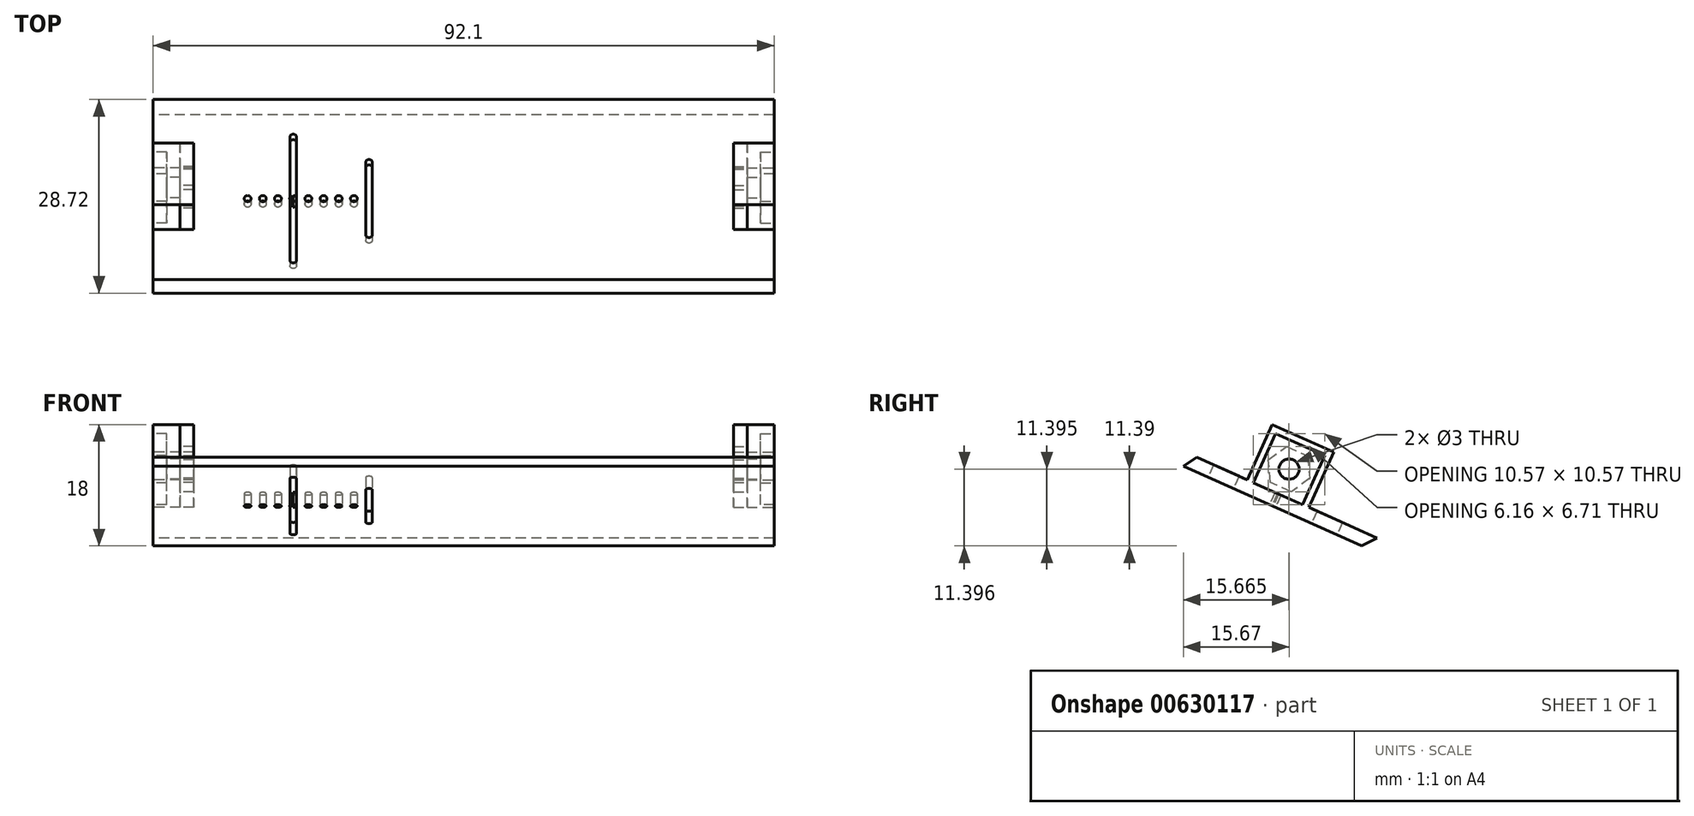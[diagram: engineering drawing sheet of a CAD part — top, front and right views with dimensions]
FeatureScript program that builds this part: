
annotation { "Feature Type Name" : "Feature", "Feature Type Description" : "" }
export const myFeature = defineFeature(function(context is Context, id is Id, definition is map)
    precondition{}
    {
        {
            var Q0;
            Q0=qCreatedBy(makeId("Right.planeOp"),FACE);
            var sketch = newSketch(context, id + "F0", { "sketchPlane" : qUnion([Q0])});
            skLineSegment(sketch, "E0.6", {"start": v(14.9, 8.68) * mm, "end": v(-11.53, 20.52) * mm});
            skLineSegment(sketch, "E1.2", {"start": v(17.19, 9.85) * mm, "end": v(-9.53, 21.81) * mm});
            skLineSegment(sketch, "E2", {"start": v(17.19, 9.85) * mm, "end": v(14.9, 8.68) * mm});
            skLineSegment(sketch, "E3", {"start": v(-9.53, 21.81) * mm, "end": v(-11.53, 20.52) * mm});
            skSolve(sketch);
        }
        {
            var Q0;
            Q0 = qSketchRegion(id + "F0", true);
            extrude(context, id + "F1", {"entities" : qUnion([Q0]), "depth" : 92.1 * mm, "offsetDistance" : 25 * mm, "symmetric" : true});
        }
        {
            var Q0;
            Q0=makeQuery(id+"F1.opExtrude","CAP_FACE",FACE,{"disambiguationData":[OSD([sQuery(id+"F0.wireOp",EDGE,"E0.6"),sQuery(id+"F0.wireOp",EDGE,"E1.2"),sQuery(id+"F0.wireOp",EDGE,"E2"),sQuery(id+"F0.wireOp",EDGE,"E3")])],"isStart":true});
            var sketch = newSketch(context, id + "F2", { "sketchPlane" : qUnion([Q0])});
            skPoint(sketch, "E4", {"position": v(-1.69, 14.6) * mm});
            skLineSegment(sketch, "E5", {"start": v(-1.69, 14.6) * mm, "end": v(-2.91, 17.34) * mm, "construction": true});
            skLineSegment(sketch, "E6", {"start": v(-2.91, 17.34) * mm, "end": v(-5.36, 22.81) * mm, "construction": true});
            skPoint(sketch, "E7", {"position": v(-4.14, 20.07) * mm});
            skCircle(sketch, "E8", {"center": v(-4.14, 20.07) * mm, "radius": 1.5 * mm});
            skCircle(sketch, "E9", {"center": v(-4.14, 20.07) * mm, "radius": 2.75 * mm, "construction": true});
            skLineSegment(sketch, "E10.bottom", {"start": v(-5.65, 16.1) * mm, "end": v(-8.1, 21.58) * mm, "construction": true});
            skLineSegment(sketch, "E10.top", {"start": v(-0.17, 18.56) * mm, "end": v(-2.63, 24.04) * mm, "construction": true});
            skLineSegment(sketch, "E10.left", {"start": v(-5.65, 16.1) * mm, "end": v(-0.17, 18.56) * mm, "construction": true});
            skLineSegment(sketch, "E10.right", {"start": v(-8.1, 21.58) * mm, "end": v(-2.63, 24.04) * mm, "construction": true});
            skLineSegment(sketch, "E11.bottom", {"start": v(-6.15, 14.79) * mm, "end": v(-9.42, 22.09) * mm});
            skLineSegment(sketch, "E11.top", {"start": v(1.15, 18.06) * mm, "end": v(-2.12, 25.36) * mm});
            skLineSegment(sketch, "E11.left", {"start": v(-6.15, 14.79) * mm, "end": v(1.15, 18.06) * mm});
            skLineSegment(sketch, "E11.right", {"start": v(-9.42, 22.09) * mm, "end": v(-2.12, 25.36) * mm});
            skLineSegment(sketch, "E12.bottom", {"start": v(-6.66, 13.47) * mm, "end": v(-10.75, 22.6) * mm});
            skLineSegment(sketch, "E12.top", {"start": v(2.47, 17.55) * mm, "end": v(-1.62, 26.68) * mm});
            skLineSegment(sketch, "E12.left", {"start": v(-6.66, 13.47) * mm, "end": v(2.47, 17.55) * mm, "construction": true});
            skLineSegment(sketch, "E12.right", {"start": v(-10.75, 22.6) * mm, "end": v(-1.62, 26.68) * mm});
            skLineSegment(sketch, "E13.0", {"start": v(-5.65, 16.1) * mm, "end": v(-2.91, 17.34) * mm, "construction": true});
            skSolve(sketch);
        }
        {
            var Q0;
            {var subQ6=sQuery(id+"F2.wireOp",EDGE,"E11.bottom");Q0=makeQuery(id+"F2.imprint","IMPRINT",FACE,{"disambiguationData":[TD([[makeQuery(id+"F2.imprint","IMPRINT",EDGE,{"derivedFrom":subQ6}),1.0]])]});}
            var Q1;
            Q1=makeQuery(id+"F2.imprint","IMPRINT",FACE,{"disambiguationData":[TD([[makeQuery(id+"F2.imprint","IMPRINT",EDGE,{"derivedFrom":sQuery(id+"F2.wireOp",EDGE,"E8")}),-1.0]])]});
            extrude(context, id + "F3", {"entities" : qUnion([Q0, Q1]), "oppositeDirection" : true, "depth" : 4 * mm, "offsetDistance" : 25 * mm});
        }
        {
            var Q0;
            Q0=makeQuery(id+"F2.imprint","IMPRINT",FACE,{"disambiguationData":[TD([[makeQuery(id+"F2.imprint","IMPRINT",EDGE,{"derivedFrom":sQuery(id+"F2.wireOp",EDGE,"E8")}),-1.0]])]});
            extrude(context, id + "F4", {"entities" : qUnion([Q0]), "operationType" : NewBodyOperationType.REMOVE, "oppositeDirection" : true, "depth" : 2 * mm, "offsetDistance" : 25 * mm});
        }
        {
            var Q0;
            Q0=makeQuery(id+"F3.opExtrude","CAP_FACE",FACE,{"disambiguationData":[OSD([sQuery(id+"F0.wireOp",EDGE,"E1.2"),sQuery(id+"F2.wireOp",EDGE,"E8"),sQuery(id+"F2.wireOp",EDGE,"E11.left"),sQuery(id+"F2.wireOp",EDGE,"E12.bottom"),sQuery(id+"F2.wireOp",EDGE,"E12.top"),sQuery(id+"F2.wireOp",EDGE,"E12.right")])],"isStart":false});
            var sketch = newSketch(context, id + "F5", { "sketchPlane" : qUnion([Q0])});
            skPoint(sketch, "E14", {"position": v(4.14, 20.07) * mm});
            skCircle(sketch, "E15.cCircle", {"center": v(4.14, 20.07) * mm, "radius": 2.92 * mm, "construction": true});
            skLineSegment(sketch, "E15.0", {"start": v(7.22, 18.7) * mm, "end": v(4.48, 16.72) * mm});
            skLineSegment(sketch, "E15.1", {"start": v(4.48, 16.72) * mm, "end": v(1.4, 18.1) * mm});
            skLineSegment(sketch, "E15.2", {"start": v(1.4, 18.1) * mm, "end": v(1.06, 21.45) * mm});
            skLineSegment(sketch, "E15.3", {"start": v(1.06, 21.45) * mm, "end": v(3.8, 23.43) * mm});
            skLineSegment(sketch, "E15.4", {"start": v(3.8, 23.43) * mm, "end": v(6.87, 22.05) * mm});
            skLineSegment(sketch, "E15.5", {"start": v(6.87, 22.05) * mm, "end": v(7.22, 18.7) * mm});
            skPoint(sketch, "E15.0.midPoint", {"position": v(5.85, 17.7) * mm});
            skLineSegment(sketch, "E16.0", {"start": v(1.06, 21.45) * mm, "end": v(7.2, 18.63) * mm, "construction": true});
            skLineSegment(sketch, "E16.1", {"start": v(7.2, 18.63) * mm, "end": v(7.22, 18.7) * mm, "construction": true});
            skLineSegment(sketch, "E17", {"start": v(-2.06, 18.47) * mm, "end": v(1.62, 26.68) * mm});
            skLineSegment(sketch, "E18", {"start": v(1.62, 26.68) * mm, "end": v(10.75, 22.6) * mm});
            skLineSegment(sketch, "E19", {"start": v(10.75, 22.6) * mm, "end": v(7.07, 14.38) * mm});
            skLineSegment(sketch, "E20", {"start": v(7.07, 14.38) * mm, "end": v(-2.06, 18.47) * mm});
            skSolve(sketch);
        }
        {
            var Q0;
            Q0 = qSketchRegion(id + "F5", true);
            extrude(context, id + "F6", {"entities" : qUnion([Q0]), "operationType" : NewBodyOperationType.ADD, "depth" : 2 * mm, "offsetDistance" : 25 * mm});
        }
        {
            var Q0;
            Q0=makeQuery(id+"F3.opExtrude","SWEPT_BODY",BODY,{"disambiguationData":[OSD([sQuery(id+"F0.wireOp",EDGE,"E1.2"),sQuery(id+"F2.wireOp",EDGE,"E8"),sQuery(id+"F2.wireOp",EDGE,"E11.left"),sQuery(id+"F2.wireOp",EDGE,"E12.bottom"),sQuery(id+"F2.wireOp",EDGE,"E12.top"),sQuery(id+"F2.wireOp",EDGE,"E12.right")])]});
            var Q1;
            Q1=qCreatedBy(makeId("Right.planeOp"),FACE);
            mirror(context, id + "F7", {"operationType" : NewBodyOperationType.ADD, "entities" : qUnion([Q0]), "mirrorPlane" : qUnion([Q1])});
        }
        {
            var Q0;
            Q0=makeQuery(id+"F1.opExtrude","SWEPT_FACE",FACE,{"disambiguationData":[OSD([sQuery(id+"F0.wireOp",EDGE,"E0.6")])]});
            var sketch = newSketch(context, id + "F8", { "sketchPlane" : qUnion([Q0])});
            skPoint(sketch, "E21", {"position": v(-46.05, 4.43) * mm});
            skPoint(sketch, "E22", {"position": v(46.05, 4.43) * mm});
            skLineSegment(sketch, "E23", {"start": v(-46.05, 4.43) * mm, "end": v(46.05, 4.43) * mm, "construction": true});
            skPoint(sketch, "E24", {"position": v(0, 4.43) * mm});
            skPoint(sketch, "E25", {"position": v(23.02, 4.43) * mm});
            skPoint(sketch, "E26", {"position": v(-46.05, 17.6) * mm});
            skLineSegment(sketch, "E27", {"start": v(-46.05, 17.6) * mm, "end": v(46.05, 17.6) * mm, "construction": true});
            skPoint(sketch, "E28", {"position": v(-23.02, 4.43) * mm});
            skEllipse(sketch, "E29", {"center": v(-23.02, 4.43) * mm, "majorRadius": 10.18 * mm, "minorRadius": 11 * mm, "majorAxis": v(0, 1), "construction": true});
            skPoint(sketch, "E30", {"position": v(-23.02, 14.6) * mm});
            skPoint(sketch, "E31.1.0.0", {"position": v(-20.77, 4.43) * mm});
            skPoint(sketch, "E31.2.0.0", {"position": v(-18.52, 4.43) * mm});
            skPoint(sketch, "E31.3.0.0", {"position": v(-16.27, 4.43) * mm});
            skPoint(sketch, "E31.4.0.0", {"position": v(-14.02, 4.43) * mm});
            skLineSegment(sketch, "E31.direction1", {"start": v(-23.02, 4.43) * mm, "end": v(-20.77, 4.43) * mm, "construction": true});
            skLineSegment(sketch, "E32", {"start": v(-23.02, 4.43) * mm, "end": v(-23.02, 14.6) * mm});
            skLineSegment(sketch, "E33", {"start": v(-20.77, 4.43) * mm, "end": v(-20.77, 14.4) * mm});
            skLineSegment(sketch, "E34", {"start": v(-18.52, 4.43) * mm, "end": v(-18.52, 13.72) * mm});
            skLineSegment(sketch, "E35", {"start": v(-16.27, 4.43) * mm, "end": v(-16.27, 12.47) * mm});
            skLineSegment(sketch, "E36", {"start": v(-14.02, 4.43) * mm, "end": v(-14.02, 10.28) * mm});
            skPoint(sketch, "E37", {"position": v(-12.03, 4.43) * mm});
            skLineSegment(sketch, "E38.MirrorCS", {"start": v(-23.02, 4.43) * mm, "end": v(-23.02, -5.75) * mm});
            skLineSegment(sketch, "E39.MirrorCS", {"start": v(-20.77, 4.43) * mm, "end": v(-20.77, -5.53) * mm});
            skLineSegment(sketch, "E40.MirrorCS", {"start": v(-18.52, 4.43) * mm, "end": v(-18.52, -4.86) * mm});
            skLineSegment(sketch, "E41.MirrorCS", {"start": v(-16.27, 4.43) * mm, "end": v(-16.27, -3.6) * mm});
            skLineSegment(sketch, "E42.MirrorCS", {"start": v(-14.02, 4.43) * mm, "end": v(-14.02, -1.42) * mm});
            skLineSegment(sketch, "E43.MirrorCS", {"start": v(-25.28, 4.43) * mm, "end": v(-25.28, 14.4) * mm});
            skLineSegment(sketch, "E44.MirrorCS", {"start": v(-25.28, 4.43) * mm, "end": v(-25.28, -5.53) * mm});
            skLineSegment(sketch, "E45.MirrorCS", {"start": v(-27.53, 4.43) * mm, "end": v(-27.53, 13.72) * mm});
            skLineSegment(sketch, "E46.MirrorCS", {"start": v(-27.53, 4.43) * mm, "end": v(-27.53, -4.86) * mm});
            skLineSegment(sketch, "E47.MirrorCS", {"start": v(-29.78, 4.43) * mm, "end": v(-29.78, 12.47) * mm});
            skLineSegment(sketch, "E48.MirrorCS", {"start": v(-29.78, 4.43) * mm, "end": v(-29.78, -3.6) * mm});
            skLineSegment(sketch, "E49.MirrorCS", {"start": v(-32.03, 4.43) * mm, "end": v(-32.03, 10.28) * mm});
            skLineSegment(sketch, "E50.MirrorCS", {"start": v(-32.03, 4.43) * mm, "end": v(-32.03, -1.42) * mm});
            skArc(sketch, "E51.0.startCap", {"start": v(-28.03, 4.43) * mm, "mid": v(-27.53, 4.93) * mm, "end": v(-27.03, 4.43) * mm});
            skArc(sketch, "E51.0.endCap", {"start": v(-27.03, -4.86) * mm, "mid": v(-27.53, -5.36) * mm, "end": v(-28.03, -4.86) * mm});
            skLineSegment(sketch, "E51.0.left", {"start": v(-27.02, 4.43) * mm, "end": v(-27.02, -4.86) * mm});
            skLineSegment(sketch, "E51.0.right", {"start": v(-28.02, 4.43) * mm, "end": v(-28.02, -4.86) * mm});
            skArc(sketch, "E51.1.startCap", {"start": v(-19.02, 4.43) * mm, "mid": v(-18.52, 4.93) * mm, "end": v(-18.02, 4.43) * mm});
            skArc(sketch, "E51.1.endCap", {"start": v(-18.02, -4.86) * mm, "mid": v(-18.52, -5.36) * mm, "end": v(-19.02, -4.86) * mm});
            skLineSegment(sketch, "E51.1.left", {"start": v(-18.03, 4.43) * mm, "end": v(-18.03, -4.86) * mm});
            skLineSegment(sketch, "E51.1.right", {"start": v(-19.02, 4.43) * mm, "end": v(-19.02, -4.86) * mm});
            skArc(sketch, "E51.2.startCap", {"start": v(-21.27, 4.43) * mm, "mid": v(-20.77, 4.93) * mm, "end": v(-20.27, 4.43) * mm});
            skArc(sketch, "E51.2.endCap", {"start": v(-20.28, -5.53) * mm, "mid": v(-20.78, -6.03) * mm, "end": v(-21.28, -5.53) * mm});
            skLineSegment(sketch, "E51.2.left", {"start": v(-20.28, 4.43) * mm, "end": v(-20.28, -5.53) * mm});
            skLineSegment(sketch, "E51.2.right", {"start": v(-21.28, 4.43) * mm, "end": v(-21.27, -5.53) * mm});
            skArc(sketch, "E51.3.startCap", {"start": v(-16.77, 4.43) * mm, "mid": v(-16.27, 4.93) * mm, "end": v(-15.77, 4.43) * mm});
            skArc(sketch, "E51.3.endCap", {"start": v(-15.77, -3.6) * mm, "mid": v(-16.27, -4.1) * mm, "end": v(-16.77, -3.6) * mm});
            skLineSegment(sketch, "E51.3.left", {"start": v(-15.78, 4.43) * mm, "end": v(-15.78, -3.6) * mm});
            skLineSegment(sketch, "E51.3.right", {"start": v(-16.77, 4.43) * mm, "end": v(-16.77, -3.6) * mm});
            skArc(sketch, "E51.4.startCap", {"start": v(-15.77, 4.43) * mm, "mid": v(-16.27, 3.93) * mm, "end": v(-16.77, 4.43) * mm});
            skArc(sketch, "E51.4.endCap", {"start": v(-16.77, 12.47) * mm, "mid": v(-16.27, 12.97) * mm, "end": v(-15.77, 12.47) * mm});
            skLineSegment(sketch, "E51.4.left", {"start": v(-16.78, 4.43) * mm, "end": v(-16.78, 12.47) * mm});
            skLineSegment(sketch, "E51.4.right", {"start": v(-15.78, 4.43) * mm, "end": v(-15.78, 12.47) * mm});
            skArc(sketch, "E51.5.startCap", {"start": v(-20.27, 4.43) * mm, "mid": v(-20.77, 3.93) * mm, "end": v(-21.27, 4.43) * mm});
            skArc(sketch, "E51.5.endCap", {"start": v(-21.28, 14.4) * mm, "mid": v(-20.78, 14.9) * mm, "end": v(-20.28, 14.4) * mm});
            skLineSegment(sketch, "E51.5.left", {"start": v(-21.27, 4.43) * mm, "end": v(-21.27, 14.4) * mm});
            skLineSegment(sketch, "E51.5.right", {"start": v(-20.28, 4.43) * mm, "end": v(-20.28, 14.4) * mm});
            skArc(sketch, "E51.7.startCap", {"start": v(-14.52, 4.43) * mm, "mid": v(-14.02, 4.93) * mm, "end": v(-13.52, 4.43) * mm});
            skArc(sketch, "E51.7.endCap", {"start": v(-13.52, -1.42) * mm, "mid": v(-14.02, -1.92) * mm, "end": v(-14.52, -1.42) * mm});
            skLineSegment(sketch, "E51.7.left", {"start": v(-13.52, 4.43) * mm, "end": v(-13.52, -1.42) * mm});
            skLineSegment(sketch, "E51.7.right", {"start": v(-14.52, 4.43) * mm, "end": v(-14.52, -1.42) * mm});
            skArc(sketch, "E51.8.startCap", {"start": v(-18.02, 4.43) * mm, "mid": v(-18.52, 3.93) * mm, "end": v(-19.02, 4.43) * mm});
            skArc(sketch, "E51.8.endCap", {"start": v(-19.02, 13.72) * mm, "mid": v(-18.52, 14.22) * mm, "end": v(-18.02, 13.72) * mm});
            skLineSegment(sketch, "E51.8.left", {"start": v(-19.02, 4.43) * mm, "end": v(-19.02, 13.72) * mm});
            skLineSegment(sketch, "E51.8.right", {"start": v(-18.03, 4.43) * mm, "end": v(-18.03, 13.72) * mm});
            skArc(sketch, "E51.9.startCap", {"start": v(-23.52, 4.43) * mm, "mid": v(-23.02, 4.93) * mm, "end": v(-22.52, 4.43) * mm});
            skArc(sketch, "E51.9.endCap", {"start": v(-22.52, -5.75) * mm, "mid": v(-23.02, -6.25) * mm, "end": v(-23.53, -5.75) * mm});
            skLineSegment(sketch, "E51.9.left", {"start": v(-22.52, 4.43) * mm, "end": v(-22.52, -5.75) * mm});
            skLineSegment(sketch, "E51.9.right", {"start": v(-23.52, 4.43) * mm, "end": v(-23.52, -5.75) * mm});
            skArc(sketch, "E51.10.startCap", {"start": v(-13.52, 4.43) * mm, "mid": v(-14.02, 3.93) * mm, "end": v(-14.52, 4.43) * mm});
            skArc(sketch, "E51.10.endCap", {"start": v(-14.52, 10.28) * mm, "mid": v(-14.02, 10.78) * mm, "end": v(-13.52, 10.28) * mm});
            skLineSegment(sketch, "E51.10.left", {"start": v(-14.52, 4.43) * mm, "end": v(-14.52, 10.28) * mm});
            skLineSegment(sketch, "E51.10.right", {"start": v(-13.52, 4.43) * mm, "end": v(-13.52, 10.28) * mm});
            skArc(sketch, "E51.11.startCap", {"start": v(-29.28, 4.43) * mm, "mid": v(-29.78, 3.93) * mm, "end": v(-30.28, 4.43) * mm});
            skArc(sketch, "E51.11.endCap", {"start": v(-30.28, 12.47) * mm, "mid": v(-29.78, 12.97) * mm, "end": v(-29.28, 12.47) * mm});
            skLineSegment(sketch, "E51.11.left", {"start": v(-30.27, 4.43) * mm, "end": v(-30.27, 12.47) * mm});
            skLineSegment(sketch, "E51.11.right", {"start": v(-29.27, 4.43) * mm, "end": v(-29.27, 12.47) * mm});
            skArc(sketch, "E51.12.startCap", {"start": v(-30.28, 4.43) * mm, "mid": v(-29.78, 4.93) * mm, "end": v(-29.28, 4.43) * mm});
            skArc(sketch, "E51.12.endCap", {"start": v(-29.28, -3.6) * mm, "mid": v(-29.78, -4.1) * mm, "end": v(-30.28, -3.6) * mm});
            skLineSegment(sketch, "E51.12.left", {"start": v(-29.27, 4.43) * mm, "end": v(-29.27, -3.6) * mm});
            skLineSegment(sketch, "E51.12.right", {"start": v(-30.27, 4.43) * mm, "end": v(-30.27, -3.6) * mm});
            skArc(sketch, "E51.13.startCap", {"start": v(-25.78, 4.43) * mm, "mid": v(-25.28, 4.93) * mm, "end": v(-24.78, 4.43) * mm});
            skArc(sketch, "E51.13.endCap", {"start": v(-24.77, -5.53) * mm, "mid": v(-25.27, -6.03) * mm, "end": v(-25.77, -5.53) * mm});
            skLineSegment(sketch, "E51.13.left", {"start": v(-24.77, 4.43) * mm, "end": v(-24.77, -5.53) * mm});
            skLineSegment(sketch, "E51.13.right", {"start": v(-25.77, 4.43) * mm, "end": v(-25.77, -5.53) * mm});
            skArc(sketch, "E51.14.startCap", {"start": v(-24.78, 4.43) * mm, "mid": v(-25.28, 3.93) * mm, "end": v(-25.78, 4.43) * mm});
            skArc(sketch, "E51.14.endCap", {"start": v(-25.77, 14.4) * mm, "mid": v(-25.27, 14.9) * mm, "end": v(-24.77, 14.4) * mm});
            skLineSegment(sketch, "E51.14.left", {"start": v(-25.77, 4.43) * mm, "end": v(-25.77, 14.4) * mm});
            skLineSegment(sketch, "E51.14.right", {"start": v(-24.77, 4.43) * mm, "end": v(-24.77, 14.4) * mm});
            skArc(sketch, "E51.15.startCap", {"start": v(-27.03, 4.43) * mm, "mid": v(-27.53, 3.93) * mm, "end": v(-28.03, 4.43) * mm});
            skArc(sketch, "E51.15.endCap", {"start": v(-28.03, 13.72) * mm, "mid": v(-27.53, 14.22) * mm, "end": v(-27.03, 13.72) * mm});
            skLineSegment(sketch, "E51.15.left", {"start": v(-28.02, 4.43) * mm, "end": v(-28.02, 13.72) * mm});
            skLineSegment(sketch, "E51.15.right", {"start": v(-27.02, 4.43) * mm, "end": v(-27.02, 13.72) * mm});
            skArc(sketch, "E51.16.startCap", {"start": v(-32.53, 4.43) * mm, "mid": v(-32.03, 4.93) * mm, "end": v(-31.53, 4.43) * mm});
            skArc(sketch, "E51.16.endCap", {"start": v(-31.53, -1.42) * mm, "mid": v(-32.03, -1.92) * mm, "end": v(-32.53, -1.42) * mm});
            skLineSegment(sketch, "E51.16.left", {"start": v(-31.52, 4.43) * mm, "end": v(-31.52, -1.42) * mm});
            skLineSegment(sketch, "E51.16.right", {"start": v(-32.52, 4.43) * mm, "end": v(-32.52, -1.42) * mm});
            skArc(sketch, "E51.17.startCap", {"start": v(-31.53, 4.43) * mm, "mid": v(-32.03, 3.93) * mm, "end": v(-32.53, 4.43) * mm});
            skArc(sketch, "E51.17.endCap", {"start": v(-32.53, 10.28) * mm, "mid": v(-32.03, 10.78) * mm, "end": v(-31.53, 10.28) * mm});
            skLineSegment(sketch, "E51.17.left", {"start": v(-32.52, 4.43) * mm, "end": v(-32.52, 10.28) * mm});
            skLineSegment(sketch, "E51.17.right", {"start": v(-31.52, 4.43) * mm, "end": v(-31.52, 10.28) * mm});
            skArc(sketch, "E51.18.startCap", {"start": v(-22.52, 4.43) * mm, "mid": v(-23.02, 3.93) * mm, "end": v(-23.52, 4.43) * mm});
            skArc(sketch, "E51.18.endCap", {"start": v(-23.53, 14.6) * mm, "mid": v(-23.02, 15.1) * mm, "end": v(-22.52, 14.6) * mm});
            skLineSegment(sketch, "E51.18.left", {"start": v(-23.52, 4.43) * mm, "end": v(-23.52, 14.6) * mm});
            skLineSegment(sketch, "E51.18.right", {"start": v(-22.52, 4.43) * mm, "end": v(-22.52, 14.6) * mm});
            skSolve(sketch);
        }
        {
            var Q0;
            Q0 = qSketchRegion(id + "F8", true);
            var Q1;
            {var subQ10=sQuery(id+"F0.wireOp",EDGE,"E2");var subQ11=sQuery(id+"F0.wireOp",EDGE,"E1.2");Q1=makeQuery(id+"F7.boolean.opBoolean","SPLIT",FACE,{"disambiguationData":[TD([makeQuery(id+"F1.opExtrude","SWEPT_FACE",FACE,{"disambiguationData":[OSD([subQ10])]})])],"derivedFrom":makeQuery(id+"F1.opExtrude","SWEPT_FACE",FACE,{"disambiguationData":[OSD([subQ11])]})});}
            extrude(context, id + "F9", {"entities" : qUnion([Q0]), "operationType" : NewBodyOperationType.REMOVE, "endBound" : BoundingType.UP_TO_SURFACE, "oppositeDirection" : true, "depth" : 25 * mm, "endBoundEntityFace" : qUnion([Q1]), "offsetDistance" : 25 * mm});
        }
    });
